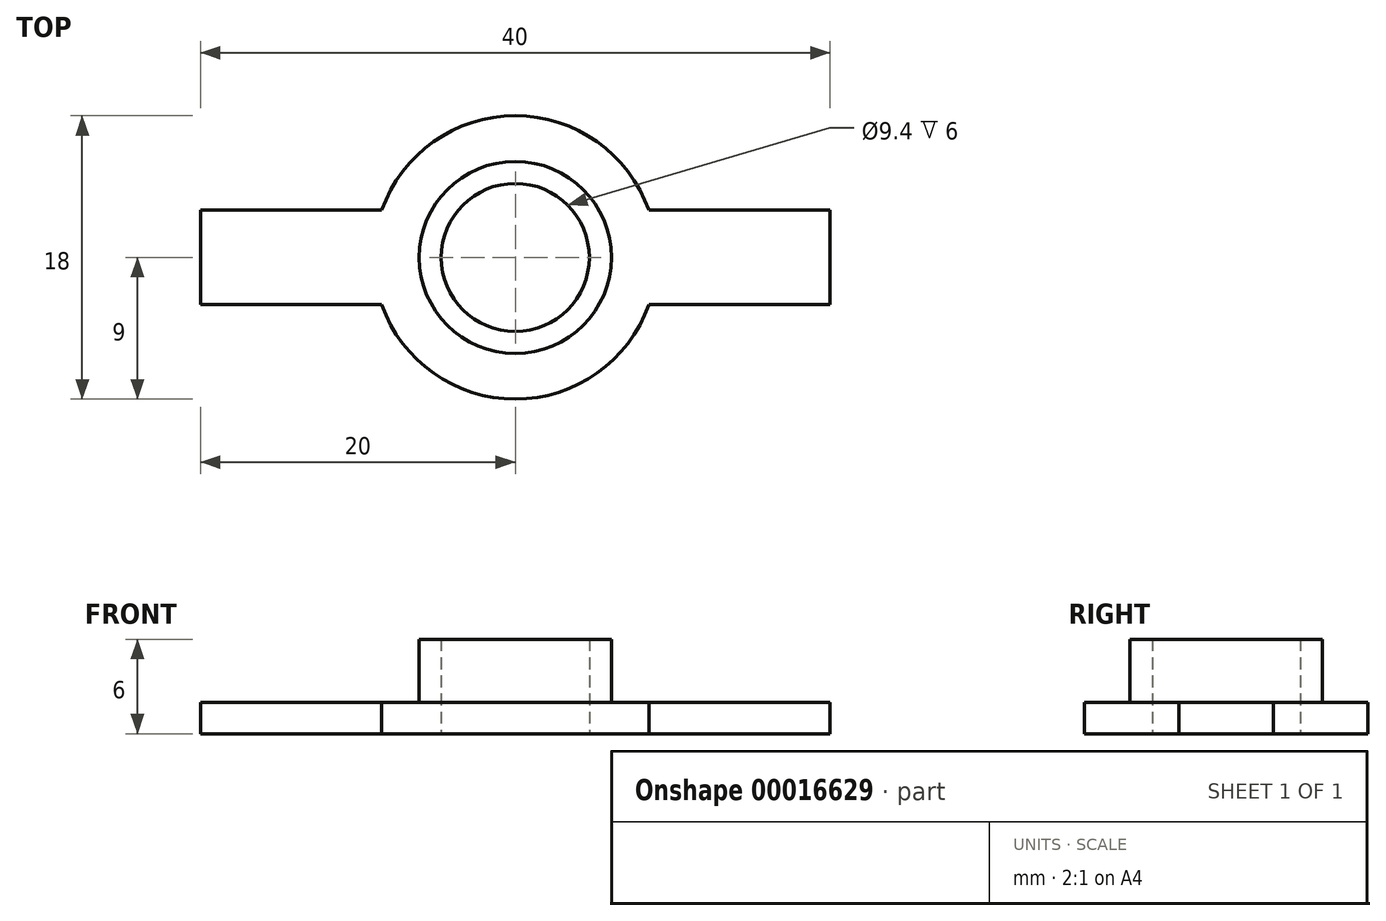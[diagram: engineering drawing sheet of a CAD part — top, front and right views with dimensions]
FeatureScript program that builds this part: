
annotation { "Feature Type Name" : "Feature", "Feature Type Description" : "" }
export const myFeature = defineFeature(function(context is Context, id is Id, definition is map)
    precondition{}
    {
        {
            var Q0;
            Q0=qCreatedBy(makeId("Top.planeOp"),FACE);
            var sketch = newSketch(context, id + "F0", { "sketchPlane" : qUnion([Q0])});
            skCircle(sketch, "E0", {"center": v(0, 0) * mm, "radius": 4.7 * mm});
            skArc(sketch, "E1", {"start": v(-8.49, -3) * mm, "mid": v(0, -9) * mm, "end": v(8.49, -3) * mm});
            skLineSegment(sketch, "E2.bottom", {"start": v(-20, 3) * mm, "end": v(-8.49, 3) * mm});
            skLineSegment(sketch, "E2.top", {"start": v(-20, -3) * mm, "end": v(-8.49, -3) * mm});
            skLineSegment(sketch, "E2.left", {"start": v(-20, 3) * mm, "end": v(-20, -3) * mm});
            skLineSegment(sketch, "E2.right", {"start": v(20, 3) * mm, "end": v(20, -3) * mm});
            skLineSegment(sketch, "E3.trimOffspring", {"start": v(8.49, 3) * mm, "end": v(20, 3) * mm});
            skLineSegment(sketch, "E4.trimOffspring", {"start": v(8.49, -3) * mm, "end": v(20, -3) * mm});
            skArc(sketch, "E5.trimOffspring", {"start": v(8.49, 3) * mm, "mid": v(0, 9) * mm, "end": v(-8.49, 3) * mm});
            skSolve(sketch);
        }
        {
            var Q0;
            Q0 = qSketchRegion(id + "F0", true);
            extrude(context, id + "F1", {"entities" : qUnion([Q0]), "depth" : 2 * mm});
        }
        {
            var Q0;
            Q0=makeQuery(id+"F1.opExtrude","CAP_FACE",FACE,{"disambiguationData":[OSD([sQuery(id+"F0.wireOp",EDGE,"E0"),sQuery(id+"F0.wireOp",EDGE,"E1")])],"isStart":false});
            var sketch = newSketch(context, id + "F2", { "sketchPlane" : qUnion([Q0])});
            skCircle(sketch, "E6", {"center": v(0, 0) * mm, "radius": 6.1 * mm});
            skCircle(sketch, "E7.0", {"center": v(0, 0) * mm, "radius": 4.7 * mm});
            skSolve(sketch);
        }
        {
            var Q0;
            Q0 = qSketchRegion(id + "F2", true);
            extrude(context, id + "F3", {"entities" : qUnion([Q0]), "operationType" : NewBodyOperationType.ADD, "depth" : 4 * mm});
        }
    });
